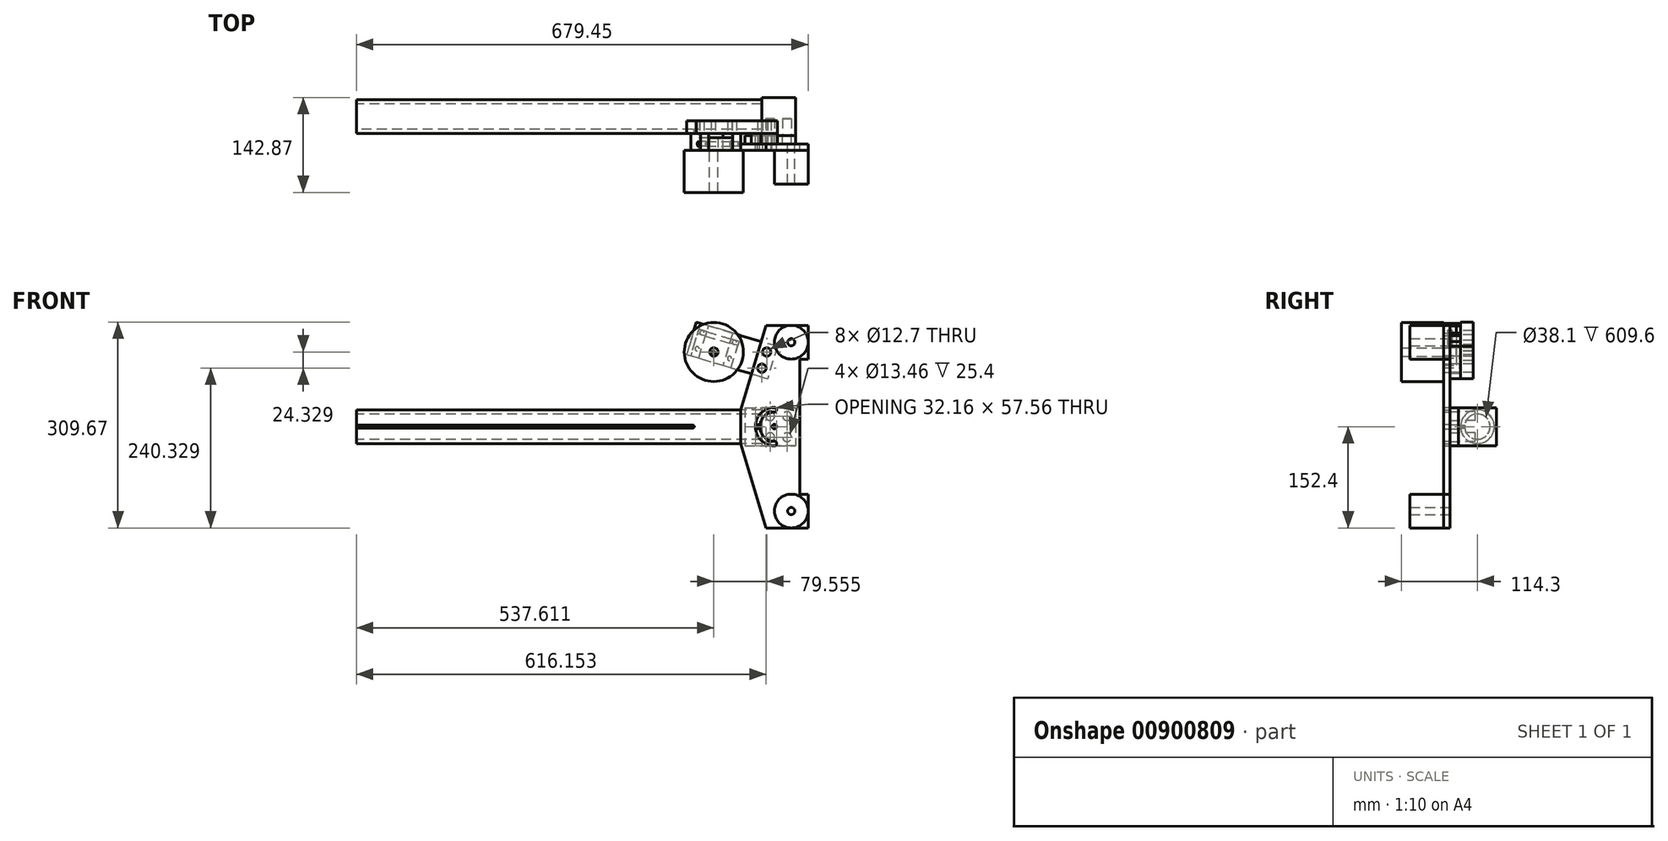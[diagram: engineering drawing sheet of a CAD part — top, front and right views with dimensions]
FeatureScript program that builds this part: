
annotation { "Feature Type Name" : "Feature", "Feature Type Description" : "" }
export const myFeature = defineFeature(function(context is Context, id is Id, definition is map)
    precondition{}
    {
        {
            var Q0;
            Q0=qCreatedBy(makeId("Right.planeOp"),FACE);
            var sketch = newSketch(context, id + "F0", { "sketchPlane" : qUnion([Q0])});
            skCircle(sketch, "E0", {"center": v(0, 0) * mm, "radius": 25.4 * mm});
            skCircle(sketch, "E1", {"center": v(0, 0) * mm, "radius": 19.05 * mm});
            skSolve(sketch);
        }
        {
            var Q0;
            Q0 = qSketchRegion(id + "F0", true);
            extrude(context, id + "F1", {"entities" : qUnion([Q0]), "depth" : 609.6 * mm, "offsetDistance" : 25.4 * mm});
        }
        {
            var Q0;
            Q0=qCreatedBy(makeId("Front.planeOp"),FACE);
            var sketch = newSketch(context, id + "F2", { "sketchPlane" : qUnion([Q0])});
            skLineSegment(sketch, "E2", {"start": v(0, 2.38) * mm, "end": v(505.62, 2.38) * mm});
            skLineSegment(sketch, "E3", {"start": v(505.62, -2.38) * mm, "end": v(0, -2.38) * mm});
            skArc(sketch, "E4", {"start": v(505.62, -2.38) * mm, "mid": v(508, 0) * mm, "end": v(505.62, 2.38) * mm});
            skLineSegment(sketch, "E5", {"start": v(0, 0) * mm, "end": v(505.62, 0) * mm, "construction": true});
            skLineSegment(sketch, "E6", {"start": v(0, 2.38) * mm, "end": v(0, -2.38) * mm});
            skSolve(sketch);
        }
        {
            var Q0;
            Q0=makeQuery(id+"F1.opExtrude","CAP_FACE",FACE,{"disambiguationData":[OSD([sQuery(id+"F0.wireOp",EDGE,"E0"),sQuery(id+"F0.wireOp",EDGE,"E1")])],"isStart":false});
            var sketch = newSketch(context, id + "F3", { "sketchPlane" : qUnion([Q0])});
            skLineSegment(sketch, "E7.bottom", {"start": v(-28.58, 28.58) * mm, "end": v(28.58, 28.58) * mm});
            skLineSegment(sketch, "E7.top", {"start": v(-28.57, -28.58) * mm, "end": v(28.58, -28.57) * mm});
            skLineSegment(sketch, "E7.left", {"start": v(-28.58, 28.58) * mm, "end": v(-28.57, -28.58) * mm});
            skLineSegment(sketch, "E7.right", {"start": v(28.58, 28.58) * mm, "end": v(28.58, -28.57) * mm});
            skLineSegment(sketch, "E8", {"start": v(-28.58, 28.58) * mm, "end": v(28.58, -28.58) * mm, "construction": true});
            skLineSegment(sketch, "E9", {"start": v(28.57, 28.58) * mm, "end": v(-28.57, -28.58) * mm, "construction": true});
            skSolve(sketch);
        }
        {
            var Q0;
            Q0 = qSketchRegion(id + "F2", true);
            extrude(context, id + "F4", {"entities" : qUnion([Q0]), "operationType" : NewBodyOperationType.REMOVE, "depth" : 25.4 * mm, "offsetDistance" : 25.4 * mm});
        }
        {
            var Q0;
            Q0 = qSketchRegion(id + "F3", true);
            extrude(context, id + "F5", {"entities" : qUnion([Q0]), "depth" : 50.8 * mm, "offsetDistance" : 25.4 * mm});
        }
        {
            var Q0;
            Q0=makeQuery(id+"F5.opExtrude","SWEPT_FACE",FACE,{"disambiguationData":[OSD([sQuery(id+"F3.wireOp",EDGE,"E7.left")])]});
            var sketch = newSketch(context, id + "F6", { "sketchPlane" : qUnion([Q0])});
            skLineSegment(sketch, "E10", {"start": v(584.2, -28.58) * mm, "end": v(660.4, -28.58) * mm});
            skLineSegment(sketch, "E11", {"start": v(660.4, -28.58) * mm, "end": v(660.4, 28.58) * mm});
            skCircle(sketch, "E12", {"center": v(622.3, 15.88) * mm, "radius": 6.73 * mm});
            skCircle(sketch, "E13", {"center": v(647.7, 15.88) * mm, "radius": 6.73 * mm});
            skCircle(sketch, "E14", {"center": v(622.3, -15.88) * mm, "radius": 6.73 * mm});
            skCircle(sketch, "E15", {"center": v(647.7, -15.88) * mm, "radius": 6.73 * mm});
            skCircle(sketch, "E16", {"center": v(628.65, 0) * mm, "radius": 3.18 * mm});
            skCircle(sketch, "E17", {"center": v(603.25, 0) * mm, "radius": 3.18 * mm});
            skLineSegment(sketch, "E18", {"start": v(577.85, 25.4) * mm, "end": v(577.85, -25.4) * mm, "construction": true});
            skLineSegment(sketch, "E19", {"start": v(577.85, -25.4) * mm, "end": v(615.95, -152.4) * mm, "construction": true});
            skLineSegment(sketch, "E20", {"start": v(615.95, -152.4) * mm, "end": v(679.45, -152.4) * mm, "construction": true});
            skLineSegment(sketch, "E21", {"start": v(679.45, -152.4) * mm, "end": v(679.45, -101.6) * mm, "construction": true});
            skLineSegment(sketch, "E22", {"start": v(679.45, -101.6) * mm, "end": v(666.75, -101.6) * mm, "construction": true});
            skLineSegment(sketch, "E23", {"start": v(666.75, -101.6) * mm, "end": v(666.75, 101.6) * mm, "construction": true});
            skLineSegment(sketch, "E24", {"start": v(666.75, 101.6) * mm, "end": v(679.45, 101.6) * mm, "construction": true});
            skLineSegment(sketch, "E25", {"start": v(679.45, 101.6) * mm, "end": v(679.45, 152.4) * mm, "construction": true});
            skLineSegment(sketch, "E26", {"start": v(679.45, 152.4) * mm, "end": v(615.95, 152.4) * mm, "construction": true});
            skLineSegment(sketch, "E27", {"start": v(615.95, 152.4) * mm, "end": v(577.85, 25.4) * mm, "construction": true});
            skLineSegment(sketch, "E28", {"start": v(577.85, 0) * mm, "end": v(666.75, 0) * mm, "construction": true});
            skCircle(sketch, "E29", {"center": v(654.05, 127) * mm, "radius": 5.36 * mm, "construction": true});
            skCircle(sketch, "E30", {"center": v(654.05, -127) * mm, "radius": 5.36 * mm, "construction": true});
            skCircle(sketch, "E31", {"center": v(628.65, 0) * mm, "radius": 3.38 * mm, "construction": true});
            skCircle(sketch, "E32", {"center": v(628.85, 25.4) * mm, "radius": 3.38 * mm, "construction": true});
            skCircle(sketch, "E33", {"center": v(628.85, -25.4) * mm, "radius": 3.38 * mm, "construction": true});
            skArc(sketch, "E34", {"start": v(628.85, 28.78) * mm, "mid": v(600.07, 0) * mm, "end": v(628.85, -28.78) * mm, "construction": true});
            skLineSegment(sketch, "E35", {"start": v(628.85, 28.78) * mm, "end": v(628.85, 22.02) * mm, "construction": true});
            skLineSegment(sketch, "E36", {"start": v(628.85, -22.02) * mm, "end": v(628.85, -28.78) * mm, "construction": true});
            skLineSegment(sketch, "E37", {"start": v(600.08, 0) * mm, "end": v(628.85, 0) * mm, "construction": true});
            skPoint(sketch, "E37.startSnap0", {"position": v(600.08, 0) * mm});
            skArc(sketch, "E38", {"start": v(628.85, 22.02) * mm, "mid": v(606.83, 0) * mm, "end": v(628.85, -22.02) * mm, "construction": true});
            skLineSegment(sketch, "E39", {"start": v(584.2, 28.58) * mm, "end": v(660.4, 28.58) * mm});
            skLineSegment(sketch, "E40", {"start": v(584.2, 28.58) * mm, "end": v(584.2, -28.58) * mm});
            skSolve(sketch);
        }
        {
            var Q0;
            Q0 = qSketchRegion(id + "F6", true);
            extrude(context, id + "F7", {"entities" : qUnion([Q0]), "depth" : 12.7 * mm, "offsetDistance" : 25.4 * mm});
        }
        {
            var Q0;
            Q0=makeQuery(id+"F6.imprint","IMPRINT",FACE,{"disambiguationData":[TD([[makeQuery(id+"F6.imprint","IMPRINT",EDGE,{"derivedFrom":sQuery(id+"F6.wireOp",EDGE,"E15")}),1.0]])]});
            var Q1;
            Q1=makeQuery(id+"F6.imprint","IMPRINT",FACE,{"disambiguationData":[TD([[makeQuery(id+"F6.imprint","IMPRINT",EDGE,{"derivedFrom":sQuery(id+"F6.wireOp",EDGE,"E13")}),1.0]])]});
            var Q2;
            Q2=makeQuery(id+"F6.imprint","IMPRINT",FACE,{"disambiguationData":[TD([[makeQuery(id+"F6.imprint","IMPRINT",EDGE,{"derivedFrom":sQuery(id+"F6.wireOp",EDGE,"E12")}),1.0]])]});
            var Q3;
            Q3=makeQuery(id+"F6.imprint","IMPRINT",FACE,{"disambiguationData":[TD([[makeQuery(id+"F6.imprint","IMPRINT",EDGE,{"derivedFrom":sQuery(id+"F6.wireOp",EDGE,"E14")}),1.0]])]});
            extrude(context, id + "F8", {"entities" : qUnion([Q0, Q1, Q2, Q3]), "operationType" : NewBodyOperationType.REMOVE, "oppositeDirection" : true, "depth" : 25.4 * mm, "offsetDistance" : 25.4 * mm});
        }
        {
            var Q0;
            Q0=makeQuery(id+"F7.opExtrude","CAP_FACE",FACE,{"disambiguationData":[OSD([sQuery(id+"F6.wireOp",EDGE,"c9rIFkiS-5h1P-935T-CxLX-Rh5mtW4yNlPI"),sQuery(id+"F6.wireOp",EDGE,"E10"),sQuery(id+"F6.wireOp",EDGE,"E11"),sQuery(id+"F6.wireOp",EDGE,"E12"),sQuery(id+"F6.wireOp",EDGE,"E13"),sQuery(id+"F6.wireOp",EDGE,"E14"),sQuery(id+"F6.wireOp",EDGE,"E15"),sQuery(id+"F6.wireOp",EDGE,"E16"),sQuery(id+"F6.wireOp",EDGE,"E17"),sQuery(id+"F6.wireOp",EDGE,"E39")])],"isStart":false});
            var sketch = newSketch(context, id + "F9", { "sketchPlane" : qUnion([Q0])});
            skLineSegment(sketch, "E41.0", {"start": v(615.95, 152.4) * mm, "end": v(577.85, 25.4) * mm});
            skLineSegment(sketch, "E42.0", {"start": v(679.45, 152.4) * mm, "end": v(615.95, 152.4) * mm});
            skLineSegment(sketch, "E43.0", {"start": v(679.45, 101.6) * mm, "end": v(679.45, 152.4) * mm});
            skLineSegment(sketch, "E44.0", {"start": v(666.75, -101.6) * mm, "end": v(666.75, 101.6) * mm});
            skLineSegment(sketch, "E45.0", {"start": v(666.75, 101.6) * mm, "end": v(679.45, 101.6) * mm});
            skLineSegment(sketch, "E46.0", {"start": v(679.45, -101.6) * mm, "end": v(666.75, -101.6) * mm});
            skLineSegment(sketch, "E47.0", {"start": v(679.45, -152.4) * mm, "end": v(679.45, -101.6) * mm});
            skLineSegment(sketch, "E48.0", {"start": v(615.95, -152.4) * mm, "end": v(679.45, -152.4) * mm});
            skCircle(sketch, "E49.0", {"center": v(654.05, -127) * mm, "radius": 5.36 * mm});
            skLineSegment(sketch, "E50.0", {"start": v(577.85, -25.4) * mm, "end": v(615.95, -152.4) * mm});
            skLineSegment(sketch, "E51.0", {"start": v(577.85, 25.4) * mm, "end": v(577.85, -25.4) * mm});
            skCircle(sketch, "E52.0", {"center": v(628.65, 0) * mm, "radius": 3.38 * mm});
            skArc(sketch, "E53.0", {"start": v(628.85, 22.02) * mm, "mid": v(606.83, 0) * mm, "end": v(628.85, -22.02) * mm});
            skArc(sketch, "E54.0", {"start": v(628.85, 28.78) * mm, "mid": v(600.07, 0) * mm, "end": v(628.85, -28.78) * mm});
            skCircle(sketch, "E55.0", {"center": v(654.05, 127) * mm, "radius": 5.36 * mm});
            skArc(sketch, "E56.0", {"start": v(628.85, 22.02) * mm, "mid": v(632.23, 25.4) * mm, "end": v(628.85, 28.78) * mm});
            skArc(sketch, "E57.0", {"start": v(628.85, -28.78) * mm, "mid": v(632.23, -25.4) * mm, "end": v(628.85, -22.02) * mm});
            skSolve(sketch);
        }
        {
            var Q0;
            Q0 = qSketchRegion(id + "F9", true);
            extrude(context, id + "F10", {"entities" : qUnion([Q0]), "depth" : 9.52 * mm, "offsetDistance" : 25.4 * mm});
        }
        {
            var Q0;
            Q0=makeQuery(id+"F10.opExtrude","CAP_FACE",FACE,{"disambiguationData":[OSD([sQuery(id+"F9.wireOp",EDGE,"E41.0"),sQuery(id+"F9.wireOp",EDGE,"E42.0"),sQuery(id+"F9.wireOp",EDGE,"E43.0"),sQuery(id+"F9.wireOp",EDGE,"E44.0"),sQuery(id+"F9.wireOp",EDGE,"E45.0"),sQuery(id+"F9.wireOp",EDGE,"E46.0"),sQuery(id+"F9.wireOp",EDGE,"E47.0"),sQuery(id+"F9.wireOp",EDGE,"E48.0"),sQuery(id+"F9.wireOp",EDGE,"E49.0"),sQuery(id+"F9.wireOp",EDGE,"E50.0"),sQuery(id+"F9.wireOp",EDGE,"E51.0"),sQuery(id+"F9.wireOp",EDGE,"E52.0"),sQuery(id+"F9.wireOp",EDGE,"E53.0"),sQuery(id+"F9.wireOp",EDGE,"E54.0"),sQuery(id+"F9.wireOp",EDGE,"E55.0"),sQuery(id+"F9.wireOp",EDGE,"E56.0"),sQuery(id+"F9.wireOp",EDGE,"E57.0")])],"isStart":false});
            var sketch = newSketch(context, id + "F11", { "sketchPlane" : qUnion([Q0])});
            skCircle(sketch, "E58.0", {"center": v(654.05, 127) * mm, "radius": 5.36 * mm});
            skCircle(sketch, "E59.0", {"center": v(654.05, -127) * mm, "radius": 5.36 * mm});
            skCircle(sketch, "E60", {"center": v(654.05, 127) * mm, "radius": 25.4 * mm});
            skCircle(sketch, "E61", {"center": v(654.05, -127) * mm, "radius": 25.4 * mm});
            skSolve(sketch);
        }
        {
            var Q0;
            Q0 = qSketchRegion(id + "F11", true);
            extrude(context, id + "F12", {"entities" : qUnion([Q0]), "depth" : 50.8 * mm, "offsetDistance" : 25.4 * mm});
        }
        {
            var Q0;
            Q0=makeQuery(id+"F10.opExtrude","CAP_FACE",FACE,{"disambiguationData":[OSD([sQuery(id+"F9.wireOp",EDGE,"E41.0"),sQuery(id+"F9.wireOp",EDGE,"E42.0"),sQuery(id+"F9.wireOp",EDGE,"E43.0"),sQuery(id+"F9.wireOp",EDGE,"E44.0"),sQuery(id+"F9.wireOp",EDGE,"E45.0"),sQuery(id+"F9.wireOp",EDGE,"E46.0"),sQuery(id+"F9.wireOp",EDGE,"E47.0"),sQuery(id+"F9.wireOp",EDGE,"E48.0"),sQuery(id+"F9.wireOp",EDGE,"E49.0"),sQuery(id+"F9.wireOp",EDGE,"E50.0"),sQuery(id+"F9.wireOp",EDGE,"E51.0"),sQuery(id+"F9.wireOp",EDGE,"E52.0"),sQuery(id+"F9.wireOp",EDGE,"E53.0"),sQuery(id+"F9.wireOp",EDGE,"E54.0"),sQuery(id+"F9.wireOp",EDGE,"E55.0"),sQuery(id+"F9.wireOp",EDGE,"E56.0"),sQuery(id+"F9.wireOp",EDGE,"E57.0")])],"isStart":true});
            var sketch = newSketch(context, id + "F13", { "sketchPlane" : qUnion([Q0])});
            skLineSegment(sketch, "E62", {"start": v(-632.98, 120.77) * mm, "end": v(-511.34, 157.27) * mm});
            skLineSegment(sketch, "E63", {"start": v(-496.74, 108.6) * mm, "end": v(-618.38, 72.12) * mm});
            skLineSegment(sketch, "E64", {"start": v(-632.98, 120.77) * mm, "end": v(-618.38, 72.12) * mm});
            skLineSegment(sketch, "E65", {"start": v(-511.34, 157.27) * mm, "end": v(-496.74, 108.6) * mm});
            skCircle(sketch, "E66", {"center": v(-536.88, 109.82) * mm, "radius": 3.38 * mm});
            skCircle(sketch, "E67", {"center": v(-519.85, 141.45) * mm, "radius": 3.18 * mm});
            skCircle(sketch, "E68", {"center": v(-512.55, 117.12) * mm, "radius": 3.18 * mm});
            skCircle(sketch, "E69", {"center": v(-561.21, 102.53) * mm, "radius": 3.18 * mm});
            skCircle(sketch, "E70", {"center": v(-568.5, 126.85) * mm, "radius": 3.18 * mm});
            skLineSegment(sketch, "E71", {"start": v(-519.85, 141.45) * mm, "end": v(-512.55, 117.12) * mm, "construction": true});
            skCircle(sketch, "E72", {"center": v(-617.17, 112.26) * mm, "radius": 6.35 * mm});
            skCircle(sketch, "E73", {"center": v(-609.87, 87.93) * mm, "radius": 6.35 * mm});
            skSolve(sketch);
        }
        {
            var Q0;
            {var subQ0=sQuery(id+"F13.wireOp",EDGE,"E64");Q0=makeQuery(id+"F13.imprint","IMPRINT",FACE,{"disambiguationData":[TD([[makeQuery(id+"F13.imprint","IMPRINT",EDGE,{"derivedFrom":subQ0}),-1.0]])]});}
            var sketch = newSketch(context, id + "F14", { "sketchPlane" : qUnion([Q0])});
            skLineSegment(sketch, "E74.0", {"start": v(-632.98, 120.77) * mm, "end": v(-618.38, 72.12) * mm});
            skLineSegment(sketch, "E75", {"start": v(-632.98, 120.77) * mm, "end": v(-608.65, 128.07) * mm});
            skLineSegment(sketch, "E76", {"start": v(-608.65, 128.07) * mm, "end": v(-594.05, 79.41) * mm});
            skLineSegment(sketch, "E77", {"start": v(-594.05, 79.41) * mm, "end": v(-618.38, 72.12) * mm});
            skCircle(sketch, "E78.0", {"center": v(-617.17, 112.26) * mm, "radius": 6.35 * mm});
            skCircle(sketch, "E79.0", {"center": v(-609.87, 87.93) * mm, "radius": 6.35 * mm});
            skSolve(sketch);
        }
        {
            var Q0;
            Q0 = qSketchRegion(id + "F14", true);
            extrude(context, id + "F15", {"entities" : qUnion([Q0]), "depth" : 15.88 * mm, "offsetDistance" : 25.4 * mm});
        }
        {
            var Q0;
            Q0 = qSketchRegion(id + "F13", true);
            extrude(context, id + "F16", {"entities" : qUnion([Q0]), "depth" : 34.92 * mm, "offsetDistance" : 25.4 * mm, "hasSecondDirection" : true, "secondDirectionOppositeDirection" : false, "secondDirectionDepth" : 15.88 * mm});
        }
        {
            var Q0;
            Q0=makeQuery(id+"F16.opExtrude","CAP_FACE",FACE,{"disambiguationData":[OSD([sQuery(id+"F13.wireOp",EDGE,"E62"),sQuery(id+"F13.wireOp",EDGE,"E63"),sQuery(id+"F13.wireOp",EDGE,"E64"),sQuery(id+"F13.wireOp",EDGE,"E65"),sQuery(id+"F13.wireOp",EDGE,"E66"),sQuery(id+"F13.wireOp",EDGE,"E67"),sQuery(id+"F13.wireOp",EDGE,"E68"),sQuery(id+"F13.wireOp",EDGE,"E69"),sQuery(id+"F13.wireOp",EDGE,"E70"),sQuery(id+"F13.wireOp",EDGE,"E72"),sQuery(id+"F13.wireOp",EDGE,"E73")])],"isStart":true});
            var sketch = newSketch(context, id + "F17", { "sketchPlane" : qUnion([Q0])});
            skLineSegment(sketch, "E80", {"start": v(517.42, 155.44) * mm, "end": v(502.82, 106.78) * mm});
            skLineSegment(sketch, "E81", {"start": v(502.82, 106.78) * mm, "end": v(514.99, 103.13) * mm});
            skLineSegment(sketch, "E82", {"start": v(514.99, 103.13) * mm, "end": v(529.58, 151.8) * mm});
            skLineSegment(sketch, "E83", {"start": v(529.58, 151.8) * mm, "end": v(517.42, 155.44) * mm});
            skCircle(sketch, "E84", {"center": v(519.85, 141.45) * mm, "radius": 3.18 * mm, "construction": true});
            skCircle(sketch, "E85", {"center": v(512.55, 117.12) * mm, "radius": 3.18 * mm, "construction": true});
            skLineSegment(sketch, "E86", {"start": v(566.08, 140.84) * mm, "end": v(551.48, 92.19) * mm});
            skLineSegment(sketch, "E87", {"start": v(551.48, 92.19) * mm, "end": v(563.64, 88.54) * mm});
            skLineSegment(sketch, "E88", {"start": v(563.64, 88.54) * mm, "end": v(578.24, 137.2) * mm});
            skLineSegment(sketch, "E89", {"start": v(578.24, 137.2) * mm, "end": v(566.08, 140.84) * mm});
            skPoint(sketch, "E90", {"position": v(568.5, 126.85) * mm});
            skSolve(sketch);
        }
        {
            var Q0;
            Q0 = qSketchRegion(id + "F17", true);
            extrude(context, id + "F18", {"entities" : qUnion([Q0]), "depth" : 25.4 * mm, "offsetDistance" : 25.4 * mm});
        }
        {
            var Q0;
            Q0=makeQuery(id+"F18.opExtrude","SWEPT_FACE",FACE,{"disambiguationData":[OSD([sQuery(id+"F17.wireOp",EDGE,"E80")])]});
            var sketch = newSketch(context, id + "F19", { "sketchPlane" : qUnion([Q0])});
            skCircle(sketch, "E91", {"center": v(41.28, 284.86) * mm, "radius": 3.38 * mm});
            skSolve(sketch);
        }
        {
            var Q0;
            Q0 = qSketchRegion(id + "F19", true);
            extrude(context, id + "F20", {"entities" : qUnion([Q0]), "operationType" : NewBodyOperationType.REMOVE, "oppositeDirection" : true, "depth" : 25.4 * mm, "offsetDistance" : 25.4 * mm});
        }
        {
            var Q0;
            Q0=makeQuery(id+"F18.opExtrude","SWEPT_FACE",FACE,{"disambiguationData":[OSD([sQuery(id+"F17.wireOp",EDGE,"E86")])]});
            var sketch = newSketch(context, id + "F21", { "sketchPlane" : qUnion([Q0])});
            skCircle(sketch, "E92.0", {"center": v(41.28, 284.86) * mm, "radius": 3.38 * mm, "construction": true});
            skCircle(sketch, "E93", {"center": v(41.28, 284.86) * mm, "radius": 3.18 * mm});
            skSolve(sketch);
        }
        {
            var Q0;
            Q0 = qSketchRegion(id + "F21", true);
            extrude(context, id + "F22", {"entities" : qUnion([Q0]), "operationType" : NewBodyOperationType.REMOVE, "oppositeDirection" : true, "depth" : 25.4 * mm, "offsetDistance" : 25.4 * mm});
        }
        {
            var Q0;
            Q0=makeQuery(id+"F18.opExtrude","SWEPT_FACE",FACE,{"disambiguationData":[OSD([sQuery(id+"F17.wireOp",EDGE,"E86")])]});
            var sketch = newSketch(context, id + "F23", { "sketchPlane" : qUnion([Q0])});
            skLineSegment(sketch, "E94.bottom", {"start": v(31.75, 297.56) * mm, "end": v(50.8, 297.56) * mm});
            skLineSegment(sketch, "E94.top", {"start": v(31.75, 246.76) * mm, "end": v(50.8, 246.76) * mm});
            skLineSegment(sketch, "E94.left", {"start": v(31.75, 297.56) * mm, "end": v(31.75, 246.76) * mm});
            skLineSegment(sketch, "E94.right", {"start": v(50.8, 297.56) * mm, "end": v(50.8, 246.76) * mm});
            skCircle(sketch, "E95", {"center": v(41.28, 284.86) * mm, "radius": 3.38 * mm});
            skSolve(sketch);
        }
        {
            var Q0;
            Q0 = qSketchRegion(id + "F23", true);
            extrude(context, id + "F24", {"entities" : qUnion([Q0]), "depth" : 38.1 * mm, "offsetDistance" : 25.4 * mm});
        }
        {
            var Q0;
            Q0=makeQuery(id+"F24.opExtrude","SWEPT_FACE",FACE,{"disambiguationData":[OSD([sQuery(id+"F23.wireOp",EDGE,"E94.right")])]});
            var sketch = newSketch(context, id + "F25", { "sketchPlane" : qUnion([Q0])});
            skCircle(sketch, "E96", {"center": v(537.61, 112.26) * mm, "radius": 6.35 * mm});
            skSolve(sketch);
        }
        {
            var Q0;
            Q0 = qSketchRegion(id + "F25", true);
            extrude(context, id + "F26", {"entities" : qUnion([Q0]), "operationType" : NewBodyOperationType.REMOVE, "oppositeDirection" : true, "depth" : 25.4 * mm, "offsetDistance" : 25.4 * mm});
        }
        {
            var Q0;
            Q0=makeQuery(id+"F13.imprint","IMPRINT",FACE,{"disambiguationData":[TD([[makeQuery(id+"F13.imprint","IMPRINT",EDGE,{"derivedFrom":sQuery(id+"F13.wireOp",EDGE,"E72")}),1.0]])]});
            var Q1;
            Q1=makeQuery(id+"F13.imprint","IMPRINT",FACE,{"disambiguationData":[TD([[makeQuery(id+"F13.imprint","IMPRINT",EDGE,{"derivedFrom":sQuery(id+"F13.wireOp",EDGE,"E73")}),1.0]])]});
            extrude(context, id + "F27", {"entities" : qUnion([Q0, Q1]), "operationType" : NewBodyOperationType.REMOVE, "oppositeDirection" : true, "depth" : 25.4 * mm, "offsetDistance" : 25.4 * mm});
        }
        {
            var Q0;
            Q0=makeQuery(id+"F24.opExtrude","SWEPT_FACE",FACE,{"disambiguationData":[OSD([sQuery(id+"F23.wireOp",EDGE,"E94.right")])]});
            var sketch = newSketch(context, id + "F28", { "sketchPlane" : qUnion([Q0])});
            skCircle(sketch, "E97", {"center": v(537.61, 112.26) * mm, "radius": 44.45 * mm});
            skCircle(sketch, "E98", {"center": v(537.61, 112.26) * mm, "radius": 6.35 * mm});
            skSolve(sketch);
        }
        {
            var Q0;
            Q0 = qSketchRegion(id + "F28", true);
            extrude(context, id + "F29", {"entities" : qUnion([Q0]), "depth" : 63.5 * mm, "offsetDistance" : 25.4 * mm});
        }
    });
